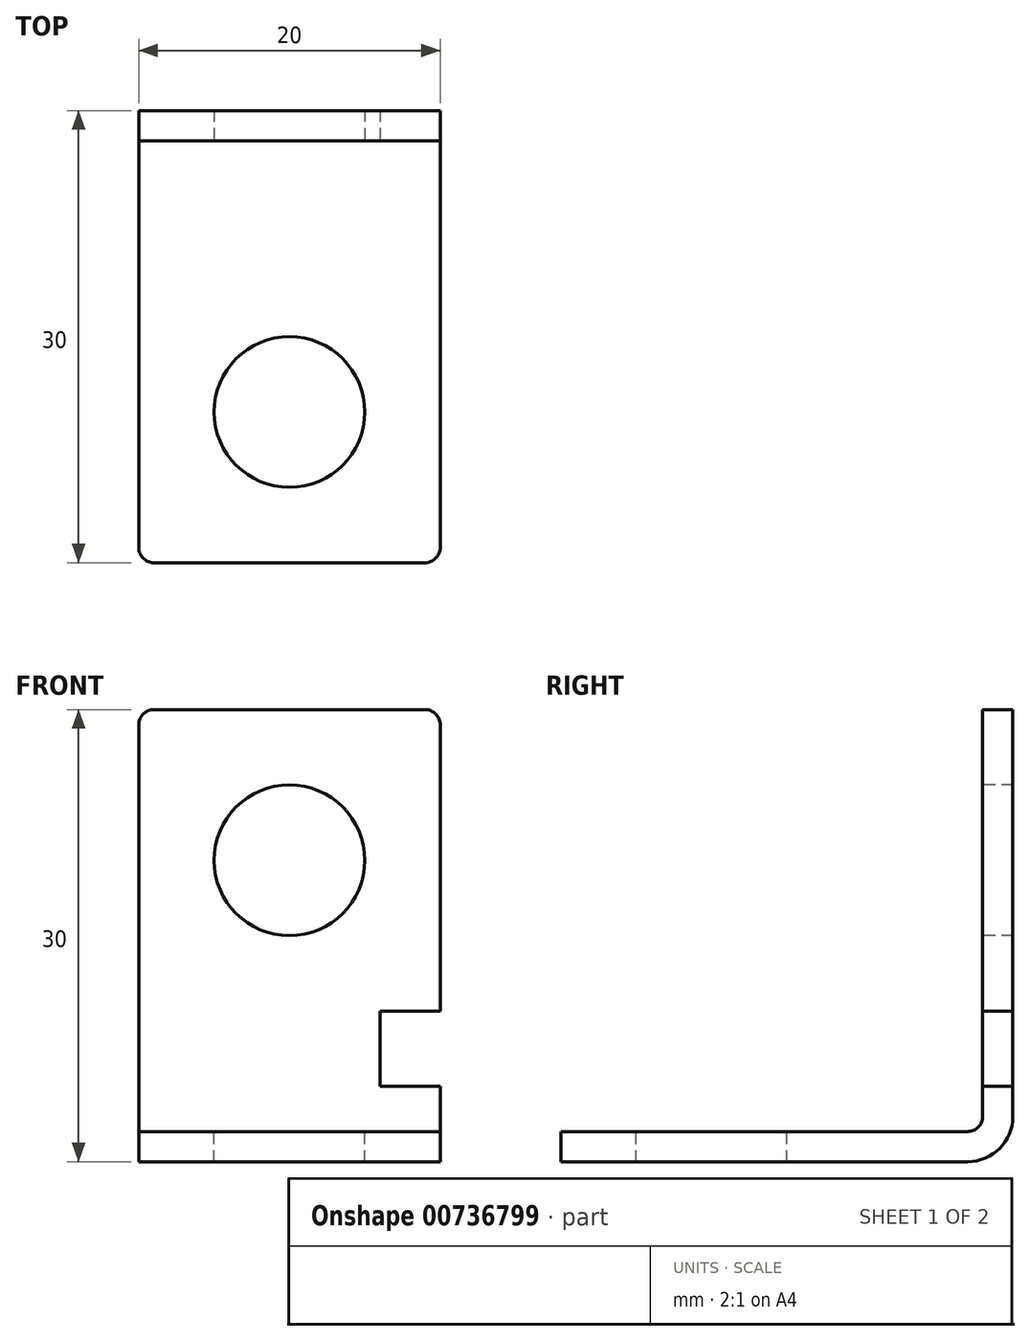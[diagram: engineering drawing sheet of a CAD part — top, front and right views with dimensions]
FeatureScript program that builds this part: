
annotation { "Feature Type Name" : "Feature", "Feature Type Description" : "" }
export const myFeature = defineFeature(function(context is Context, id is Id, definition is map)
    precondition{}
    {
        {
            var Q0;
            Q0=qCreatedBy(makeId("Right.planeOp"),FACE);
            var sketch = newSketch(context, id + "F0", { "sketchPlane" : qUnion([Q0])});
            skLineSegment(sketch, "E0", {"start": v(-22.28, 0) * mm, "end": v(-22.28, 2) * mm});
            skLineSegment(sketch, "E1", {"start": v(-22.28, 2) * mm, "end": v(4.72, 2) * mm});
            skLineSegment(sketch, "E2", {"start": v(-22.28, 0) * mm, "end": v(4.72, 0) * mm});
            skArc(sketch, "E3", {"start": v(4.72, 0) * mm, "mid": v(6.84, 0.88) * mm, "end": v(7.72, 3) * mm});
            skLineSegment(sketch, "E4", {"start": v(7.72, 3) * mm, "end": v(7.72, 30) * mm});
            skLineSegment(sketch, "E5", {"start": v(7.72, 30) * mm, "end": v(5.72, 30) * mm});
            skLineSegment(sketch, "E6", {"start": v(5.72, 3) * mm, "end": v(5.72, 30) * mm});
            skArc(sketch, "E7", {"start": v(4.72, 2) * mm, "mid": v(5.42, 2.3) * mm, "end": v(5.72, 3) * mm});
            skSolve(sketch);
        }
        {
            var Q0;
            Q0 = qSketchRegion(id + "F0", true);
            extrude(context, id + "F1", {"entities" : qUnion([Q0]), "depth" : 20 * mm, "offsetDistance" : 25 * mm});
        }
        {
            var Q0;
            Q0=makeQuery(id+"F1.opExtrude","SWEPT_FACE",FACE,{"disambiguationData":[OSD([sQuery(id+"F0.wireOp",EDGE,"E1")])]});
            var sketch = newSketch(context, id + "F2", { "sketchPlane" : qUnion([Q0])});
            skCircle(sketch, "E8", {"center": v(10, -12.28) * mm, "radius": 5 * mm});
            skSolve(sketch);
        }
        {
            var Q0;
            Q0 = qSketchRegion(id + "F2", true);
            extrude(context, id + "F3", {"entities" : qUnion([Q0]), "operationType" : NewBodyOperationType.REMOVE, "oppositeDirection" : true, "depth" : 25 * mm, "offsetDistance" : 25 * mm});
        }
        {
            var Q0;
            Q0=makeQuery(id+"F1.opExtrude","SWEPT_FACE",FACE,{"disambiguationData":[OSD([sQuery(id+"F0.wireOp",EDGE,"E6")])]});
            var sketch = newSketch(context, id + "F4", { "sketchPlane" : qUnion([Q0])});
            skCircle(sketch, "E9", {"center": v(10, 20) * mm, "radius": 5 * mm});
            skLineSegment(sketch, "E10", {"start": v(20, 10) * mm, "end": v(16, 10) * mm});
            skLineSegment(sketch, "E11", {"start": v(16, 10) * mm, "end": v(16, 5) * mm});
            skLineSegment(sketch, "E12", {"start": v(16, 5) * mm, "end": v(20, 5) * mm});
            skLineSegment(sketch, "E13", {"start": v(20, 5) * mm, "end": v(20, 10) * mm});
            skSolve(sketch);
        }
        {
            var Q0;
            Q0 = qSketchRegion(id + "F4", true);
            extrude(context, id + "F5", {"entities" : qUnion([Q0]), "operationType" : NewBodyOperationType.REMOVE, "oppositeDirection" : true, "depth" : 25 * mm, "offsetDistance" : 25 * mm});
        }
        {
            var Q0;
            Q0=makeQuery(id+"F1.opExtrude","CAP_EDGE",EDGE,{"disambiguationData":[OSD([sQuery(id+"F0.wireOp",EDGE,"E5")])],"isStart":false});
            var Q1;
            Q1=makeQuery(id+"F1.opExtrude","CAP_EDGE",EDGE,{"disambiguationData":[OSD([sQuery(id+"F0.wireOp",EDGE,"E0")])],"isStart":false});
            var Q2;
            Q2=makeQuery(id+"F1.opExtrude","CAP_EDGE",EDGE,{"disambiguationData":[OSD([sQuery(id+"F0.wireOp",EDGE,"E0")])],"isStart":true});
            var Q3;
            Q3=makeQuery(id+"F1.opExtrude","CAP_EDGE",EDGE,{"disambiguationData":[OSD([sQuery(id+"F0.wireOp",EDGE,"E5")])],"isStart":true});
            fillet(context, id + "F6", {"entities" : qUnion([Q0, Q1, Q2, Q3]), "radius" : 1 * mm, "tangentPropagation" : true, "allowEdgeOverflow" : false});
        }
    });
